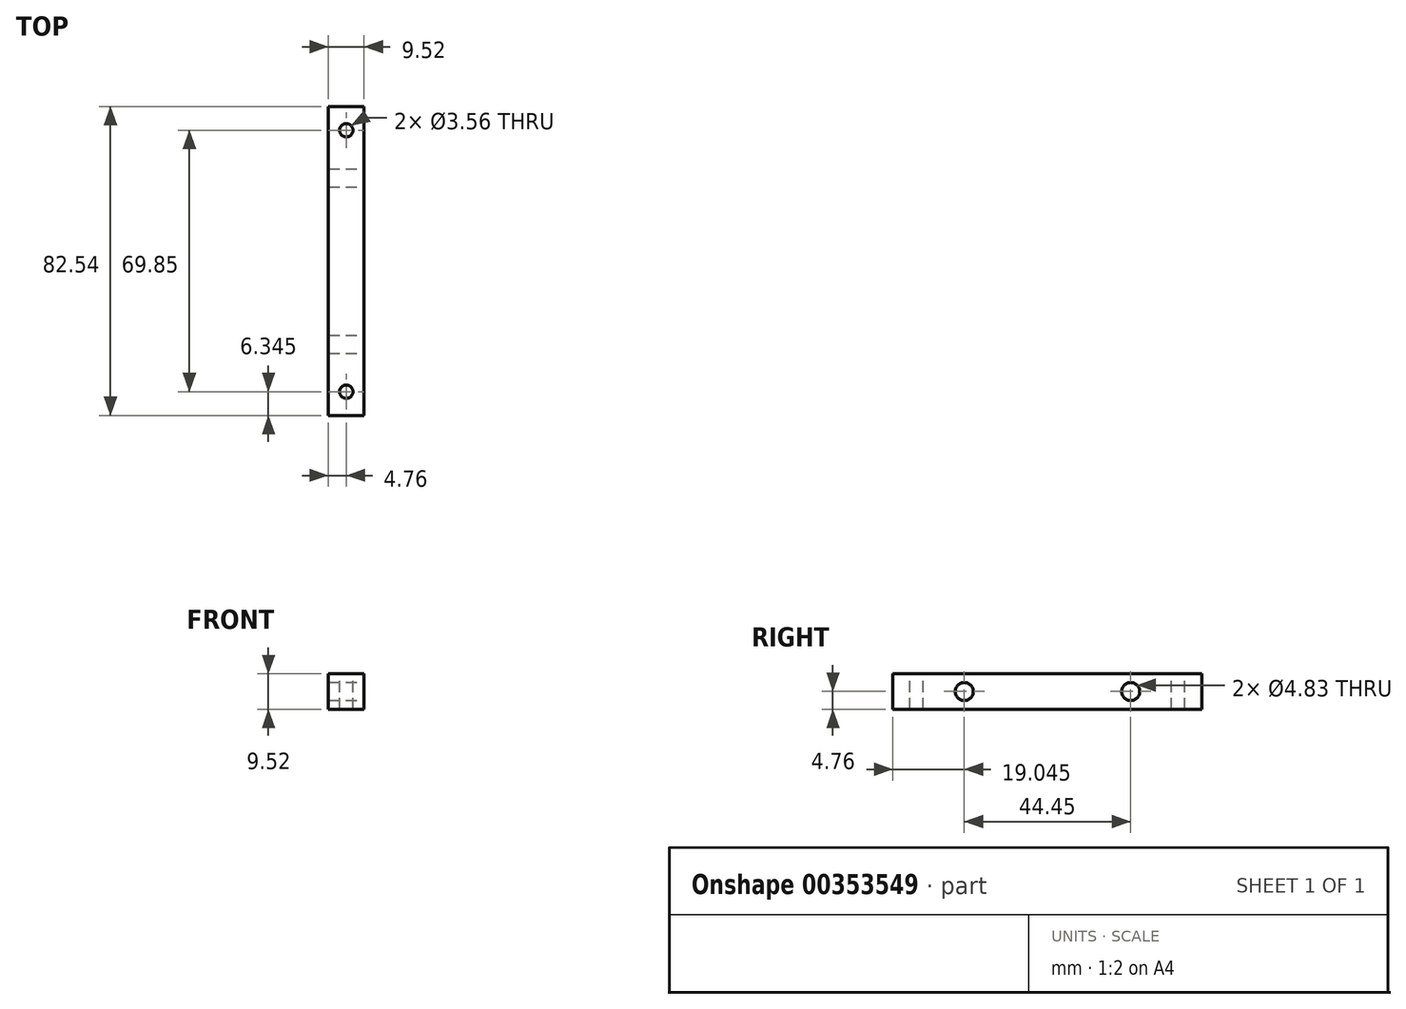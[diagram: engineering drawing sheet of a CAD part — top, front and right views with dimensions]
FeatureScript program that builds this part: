
annotation { "Feature Type Name" : "Feature", "Feature Type Description" : "" }
export const myFeature = defineFeature(function(context is Context, id is Id, definition is map)
    precondition{}
    {
        {
            var Q0;
            Q0=qCreatedBy(makeId("Front.planeOp"),FACE);
            var sketch = newSketch(context, id + "F0", { "sketchPlane" : qUnion([Q0])});
            skLineSegment(sketch, "E0.bottom", {"start": v(-4.76, 4.76) * mm, "end": v(4.76, 4.76) * mm});
            skLineSegment(sketch, "E0.top", {"start": v(-4.76, -4.76) * mm, "end": v(4.76, -4.76) * mm});
            skLineSegment(sketch, "E0.left", {"start": v(-4.76, 4.76) * mm, "end": v(-4.76, -4.76) * mm});
            skLineSegment(sketch, "E0.right", {"start": v(4.76, 4.76) * mm, "end": v(4.76, -4.76) * mm});
            skPoint(sketch, "E0.middle", {"position": v(0, 0) * mm});
            skSolve(sketch);
        }
        {
            var Q0;
            Q0 = qSketchRegion(id + "F0", true);
            extrude(context, id + "F1", {"entities" : qUnion([Q0]), "depth" : 82.55 * mm, "symmetric" : true});
        }
        {
            var Q0;
            Q0=makeQuery(id+"F1.opExtrude","SWEPT_FACE",FACE,{"disambiguationData":[OSD([sQuery(id+"F0.wireOp",EDGE,"E0.bottom")])]});
            var sketch = newSketch(context, id + "F2", { "sketchPlane" : qUnion([Q0])});
            skLineSegment(sketch, "E1", {"start": v(0, 0) * mm, "end": v(0, -34.93) * mm, "construction": true});
            skCircle(sketch, "E2", {"center": v(0, -34.93) * mm, "radius": 1.78 * mm});
            skSolve(sketch);
        }
        {
            var Q0;
            Q0 = qSketchRegion(id + "F2", true);
            extrude(context, id + "F3", {"entities" : qUnion([Q0]), "operationType" : NewBodyOperationType.REMOVE, "endBound" : BoundingType.THROUGH_ALL, "oppositeDirection" : true, "depth" : 25.4 * mm});
        }
        {
            var Q0;
            Q0=makeQuery(id+"F1.opExtrude","SWEPT_FACE",FACE,{"disambiguationData":[OSD([sQuery(id+"F0.wireOp",EDGE,"E0.bottom")])]});
            var sketch = newSketch(context, id + "F4", { "sketchPlane" : qUnion([Q0])});
            skLineSegment(sketch, "E3", {"start": v(0, 0) * mm, "end": v(0, 34.93) * mm, "construction": true});
            skCircle(sketch, "E4", {"center": v(0, 34.93) * mm, "radius": 1.78 * mm});
            skSolve(sketch);
        }
        {
            var Q0;
            Q0 = qSketchRegion(id + "F4", true);
            extrude(context, id + "F5", {"entities" : qUnion([Q0]), "operationType" : NewBodyOperationType.REMOVE, "endBound" : BoundingType.THROUGH_ALL, "oppositeDirection" : true, "depth" : 25.4 * mm});
        }
        {
            var Q0;
            Q0=makeQuery(id+"F1.opExtrude","SWEPT_FACE",FACE,{"disambiguationData":[OSD([sQuery(id+"F0.wireOp",EDGE,"E0.right")])]});
            var sketch = newSketch(context, id + "F6", { "sketchPlane" : qUnion([Q0])});
            skLineSegment(sketch, "E5", {"start": v(0, 0) * mm, "end": v(-22.23, 0) * mm, "construction": true});
            skCircle(sketch, "E6", {"center": v(-22.23, 0) * mm, "radius": 2.41 * mm});
            skSolve(sketch);
        }
        {
            var Q0;
            Q0 = qSketchRegion(id + "F6", true);
            extrude(context, id + "F7", {"entities" : qUnion([Q0]), "operationType" : NewBodyOperationType.REMOVE, "endBound" : BoundingType.THROUGH_ALL, "oppositeDirection" : true, "depth" : 25.4 * mm});
        }
        {
            var Q0;
            Q0=makeQuery(id+"F1.opExtrude","SWEPT_FACE",FACE,{"disambiguationData":[OSD([sQuery(id+"F0.wireOp",EDGE,"E0.right")])]});
            var sketch = newSketch(context, id + "F8", { "sketchPlane" : qUnion([Q0])});
            skLineSegment(sketch, "E7", {"start": v(0, 0) * mm, "end": v(22.22, 0) * mm, "construction": true});
            skCircle(sketch, "E8", {"center": v(22.22, 0) * mm, "radius": 2.41 * mm});
            skSolve(sketch);
        }
        {
            var Q0;
            Q0 = qSketchRegion(id + "F8", true);
            extrude(context, id + "F9", {"entities" : qUnion([Q0]), "operationType" : NewBodyOperationType.REMOVE, "endBound" : BoundingType.THROUGH_ALL, "oppositeDirection" : true, "depth" : 25.4 * mm});
        }
    });
